# Revit family: Screens-Beam_Mounted-Teknion-JNSFSB-Floor_Screen-R20161
name_source: partatom
category: Furniture
revit_build: Autodesk Revit Architecture 2016 (Build: 20150714_1515(x64)
units: mm (PartAtom-declared; Revit-internal decimal feet)

## family parameters
Always vertical = Yes
Cut with Voids When Loaded = No
OmniClass Number = 23.40.20.00
OmniClass Title = General Furniture and Specialties
Room Calculation Point = No
Shared = Yes
Work Plane-Based = No

## types (4) — shared parameters
Assembly Code = E2020200
Manufacturer = Teknion
Manufacturer Fax = 416.661.4586
Part Number = JNSFSB
Product Documentation Link = http://www.teknion.com
Product Line = Expansion Cityline
Product Page URL = http://www.teknion.com
Series = Expansion Cityline
Sustainability Data = http://www.teknion.com
URL = www.teknion.com
Unit Weight URL = http://www.teknion.com
Warranty = http://www.teknion.com

## per-type parameters (varying)
| type | Description | Model | Standard With |
| Both Sides Width Extension | Floor Screen - Beam-Mounted, Both Sides Width Extension, Standard Corner Detail, No Cable Pass-Through | JNSFSB__BS_N | No |
| One Side - Left Width Extension | Floor Screen - Beam-Mounted, One Side - Left Width Extension, Standard Corner Detail, No Cable Pass-Through | JNSFSB__LS_N | No |
| One Side - Right Width Extension | Floor Screen - Beam-Mounted, One Side - Right Width Extension, Standard Corner Detail, No Cable Pass-Through | JNSFSB__RS_N | No |
| Standard Width | Floor Screen - Beam-Mounted, Standard Width, Standard Corner Detail, No Cable Pass-Through | JNSFSB__SS_N | Yes |

type visibility flags (boolean, named after types; folded from table):
- Both Sides Width Extension: Yes: Both Sides Width Extension
- One Side - Left Width Extension: Yes: One Side - Left Width Extension
- One Side - Right Width Extension: Yes: One Side - Right Width Extension
- Standard Width: Yes: (none)

## geometry (parser evidence)
native form markers: Blend x2, Sweep x1
no freeform markers — native parametric forms only
